# Revit family: PANZERI_GINEVRA_CEILING_LIGHT
name_source: partatom
category: Lighting Fixtures
revit_build: Autodesk Revit 2018 (Build: 20190510_1515(x64)
units: mm (PartAtom-declared; Revit-internal decimal feet)

## family parameters
Cut with Voids When Loaded = No
Host = Face
Light Source = Yes
OmniClass Number = 23.80.70.00
OmniClass Title = Lighting
Part Type = Normal
Room Calculation Point = Yes
Round Connector Dimension = Use Diameter
Shared = No

## types (4) — shared parameters
ACCESSORIES = DRIVER: integrated included
AVAILABLE FINISHES = Structure: mat black and gold or white and gold; Canopy: white or mat black. CUSTOM finishes available only on request.
Apparent Load = 0 VA
BIM BADGE = https://bim.archiproducts.com
BODY AND LIGHT SOURCE = 1_Body_LightSource_PANZERI_GINEVRA_CEILING_LIGHT : Ø53cm_3000K
CANOPY_VISIBILITY = Yes
COLLECTION = GINEVRA
COLOR RENDERING INDEX = Ra>90
Color Filter = 16777215
DESIGNER = Christian Burtolf
Default Elevation = 1219 mm
Description = Ceiling or wall lighting fixture for interiors, with direct light emission.
Dimming Lamp Color Temperature Shift = <None>
ENERGY EFFICIENCY CLASS = N/D
FREQUENCY = 0 Hz
FREQUENCY RANGE = 50/60Hz
INSTALLATION INSTRUCTIONS = https://panzeri.it
IP RATING = IP20
LAMP MATERIAL = PANZERI_POLYCARBONATE_OPALINE_SCREEN_Light_on
Lamp = LED
Light Source Symbol Size = 300 mm
MATERIAL DESCRIPTION = Turned aluminium structure in polyacrylic paint. Pickled sheet metal wiring support plate in polyacrylic paint. Moulded polycarbonate micro-prismatic diffuser.
Manufacturer = PANZERI
Model = GINEVRA WALL-CEILING
POWER SUPPLY = 220-240V AC
PRODUCT SHEET = https://www.archiproducts.com
STRUCTURE MATERIAL = PANZERI_ALUMINIUM_POLYACRYLIC_PAINT_MAT_BLACK_06
TECHNICAL SHEET = https://panzeri.it
Tilt Angle = -90.00°
Type Comments = Direct light emission.
URL = https://panzeri.it
USAGE = INDOOR - CEILING/WALL
VOLTAGE = 0 V

## per-type parameters (varying)
| type | DIAMETER | HEIGHT | LIGHTING SPECIFICATION | PACKAGING | PRODUCT CODE | Photometric Note | Photometric Web File | WATTAGE | WEIGHT |
| Ø53cm_3000K_Black | 530 mm | 110 mm | LED 25W / 3000K / Ra>90 / 1877lm / 220-240V AC / dimmable (DALI/Push DIM) | 20,0 x 62,0 x 62,0 cm | P09280.050.0402 |  | Ginevra P092__.050.0402-3100.IES | 36 W | 5.08 kg |
| Ø80cm_3000K_Black | 800 mm | 140 mm | LED 71W / 3000K / Ra>90 / 6743lm / 220-240V AC / dimmable (DALI/Push DIM) | 18,0 x 90,0 x 90,0 cm | P09280.080.0402 |  | Ginevra P092__.080.0402-8857.IES | 71 W | 10.70 kg |
| Ø53cm_TunableWhiteLight_Black | 530 mm | 110 mm | LED 30W / 2700-6500K / Ra>90 / 1794lm min - 2046lm max / 220-240V AC / tunable white | 20,0 x 62,0 x 62,0 cm | P09280.050.9017 | This type has a tunable white light, You can change the Initial Color and Initial Intensity respecting the Range written in the LIGHTING SPECIFICATION. | Ginevra P092__.050.0402-3100.IES | 30 W | 5.08 kg |
| Ø80cm_TunableWhiteLight_Black | 800 mm | 140 mm | LED 69W / 2700-6500K / Ra>90 / 6518lm min - 7190lm max / 220-240V AC / tunable white | 18,0 x 90,0 x 90,0 cm | P09280.080.9017 | This type has a tunable white light, You can change the Initial Color and Initial Intensity respecting the Range written in the LIGHTING SPECIFICATION. | Ginevra P092__.080.0402-8857.IES | 69 W | 10.70 kg |

## geometry (parser evidence)
native form markers: Sweep x7
no freeform markers — native parametric forms only
